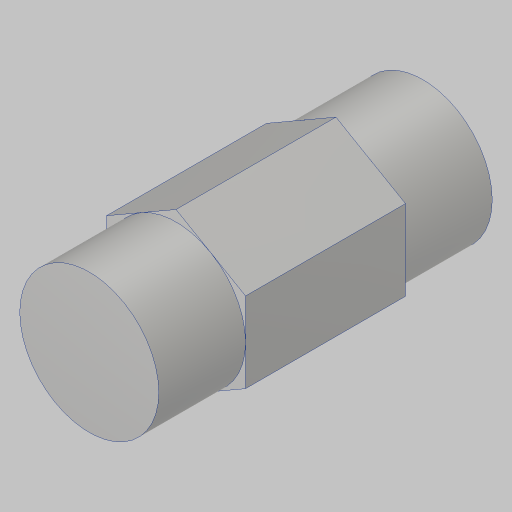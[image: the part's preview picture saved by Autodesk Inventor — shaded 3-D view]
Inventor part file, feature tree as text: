
AUTODESK INVENTOR PART (.ipt)
format: ipt  version: 2023.5 (Build 275446000, 446)  size: 196,096 bytes
history: native  units: in
note: dims shown in document units (in); Inventor stores cm internally (conversion verified against a paired STEP export)
features: extrude x2, mirror x1, projected_geometry x1
ambient origin geometry x8: Origin, YZ Plane, XZ Plane, XY Plane, X Axis, Y Axis, Z Axis, Center Point
bodies: Solid1 (feature_tree)
feature tree (4):
  extrude  "Extrusion1"  TaperAngle=0.0deg  [1 undecoded]
  extrude  "Extrusion2"  TaperAngle=0.0deg  [1 undecoded]
  mirror  "Mirror1"
  projected_geometry  "Projected Loop1"
note: 2 required parameter values undecoded (feature->parameter linkage not recoverable at this tier; creation-order binding heuristic only, values carry confidence <= 0.55)
